# Revit family: Обратный клапан 2621 00 (01)
name_source: partatom
category: Rohrzubehör
units: mm (PartAtom-declared; Revit-internal decimal feet)

## family parameters
Arbeitsebenenbasiert = Nein
Beim Laden mit Abzugskörper schneiden = Nein
Bemaßung runder Anschluss = Durchmesser verwenden
Gemeinsam genutzt = Nein
Immer vertikal = Ja
OmniClass-Nummer = 23.65.55.14
OmniClass-Titel = Valves for Liquid Services
Teiletyp = Unterbricht

## types (1)
- Обратный клапан 2621 00 (01)
    G2 = 5 mm  [stored 0.0164042 ft]
    H01 = 9.5 mm  [stored 0.031168 ft]
    H03 = 9.5 mm  [stored 0.031168 ft]
    Hersteller = Herz-Armaturen GmbH
    Nennweite IG = 10 mm  [stored 0.0328084 ft]
    SCRNCODE = 05;17;02
    SCRNSEQ = AWI;AWI_TYP="1007";2
    SCTWCODE = 04;14;02
    SCTWSEQ = FW;SBT_TYP_FW="108";2
    URL = www.herz-armaturen.ru
    Корпус = Латунь
    Макс. рабочая температура = 110 °C
    Макс. рабочее давление = 1000000.0 Pa

note: [stored X ft] marks values corroborated as IEEE doubles in the binary element streams (Revit-internal decimal feet)
